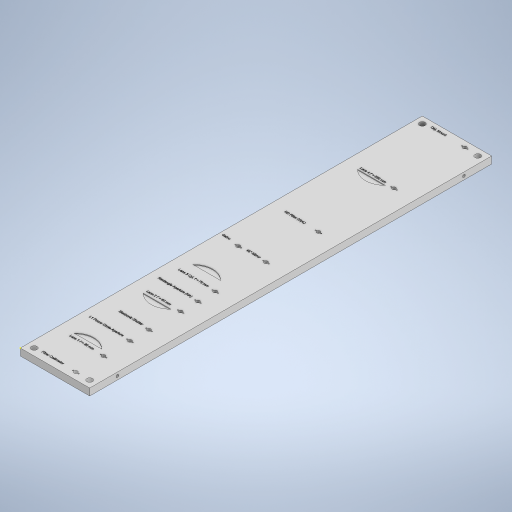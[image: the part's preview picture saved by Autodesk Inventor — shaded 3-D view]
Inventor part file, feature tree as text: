
AUTODESK INVENTOR PART (.ipt)
format: ipt  version: 2024.2 (Build 282272000, 272)  size: 3,316,224 bytes
history: native  units: in
note: dims shown in document units (in); Inventor stores cm internally (conversion verified against a paired STEP export)
features: extrude x7, sketch x5, other x2, hole x2
ambient origin geometry x8: Origin, YZ Plane, XZ Plane, XY Plane, X Axis, Y Axis, Z Axis, Center Point
bodies: Solid1 (feature_tree)
feature tree (16):
  extrude  "Extrusion1"  Depth=5.0in
  other  "Board Mounting Holes"
  extrude  "Extrusion2"  Depth=0.5in
  extrude  "Extrusion3"  Depth=0.5in
  other  "Element Holes"
  extrude  "Extrusion4"  Depth=0.5in
  extrude  "Extrusion5"  Depth=0.75in
  extrude  "Extrusion6"  Depth=0.5in
  extrude  "Extrusion7"  Depth=0.75in
  sketch  "Sketch6"  dims[d5=0.5in d6=0.5in]
  hole  "Hole1"  [1 undecoded]
  hole  "Hole2"  [1 undecoded]
  sketch  "Sketch1"  dims[d0=29.0in d1=5.0in]
  sketch  "Sketch5"  dims[d2=0.5in d3=0.0in d4=0.5in]
  sketch  "Sketch7"  dims[d7=0.5in d8=0.5in]
  sketch  "Sketch8"  dims[d9=0.4in d10=0.25in d11=0.5in d12=0.4in d13=0.3in d14=0.0in d15=0.5in d16=0.0in d17=1.5in d18=0.5in d19=0.197in d20=0.197in d21=0.25in d22=0.08in d23=0.08in d24=2.0in d25=1.898in d26=3.663in d27=1.25in d28=1.25in d29=3.667in d31=5.278in d32=6.311in d33=9.229in d34=5.107in d35=0.197in d36=0.197in d37=0.25in d38=0.08in d39=0.08in d40=0.197in d41=0.197in d42=0.25in d43=0.08in d44=0.08in d45=0.197in d46=0.197in d47=0.25in d48=0.08in d49=0.08in d50=0.197in d51=0.197in d52=0.25in d53=0.08in d54=0.08in d55=0.197in d56=0.197in d57=0.25in d58=0.08in d59=0.08in d60=0.197in d61=0.197in d62=0.25in d63=0.08in d64=0.08in d65=0.197in d66=0.197in d67=0.25in d68=0.08in d69=0.08in d70=0.197in d71=0.197in d72=0.25in d73=0.08in d74=0.08in d75=0.197in d76=0.197in d77=0.25in d78=0.08in d79=0.08in d80=0.197in d81=0.197in d82=0.25in d83=0.08in d84=0.08in d85=2.0in d86=1.0in d87=1.0in d88=1.0in d89=0.197in d90=0.197in d91=0.25in d92=0.08in d93=0.08in d94=0.197in d95=0.197in d96=0.25in d97=0.08in d98=0.08in d99=0.197in d100=0.197in d101=0.25in d102=0.08in d103=0.08in d104=0.197in d105=0.197in d106=0.25in d107=0.08in d108=0.08in d113=0.5in d114=2.0in d115=2.0in d116=2.0in d117=2.0in d118=2.0in d119=2.0in d120=2.0in d121=2.0in d122=2.0in d123=2.0in d125=1.378in d126=1.378in d127=1.378in d128=1.378in d129=1.378in d130=0.05in d131=0.0in d132=0.175in d133=0.0in d134=0.5in d135=0.0in d136=2.0in d137=1.898in d138=3.663in d139=1.25in d140=1.25in d141=3.667in d142=5.278in d144=1.58in d145=9.229in d146=5.107in d147=2.0in d148=1.0in d149=1.0in d150=1.0in d151=0.4in d152=0.4in d153=0.4in d154=0.4in d155=0.4in d156=0.4in d157=0.4in d158=0.4in d159=0.4in d160=0.4in d161=0.4in d162=0.4in d163=0.4in d164=0.4in d165=0.4in d166=0.3in d167=0.0in d168=1.5in d169=0.197in d170=0.197in d171=0.25in d172=0.08in d173=0.08in d174=1.5in d175=0.4in d176=6.311in d177=6.311in d178=6.311in d184=1.378in d185=0.197in d186=0.197in d187=0.25in d188=0.08in d189=0.08in d190=1.378in d191=2.0in d192=2.0in d193=0.196in d194=0.75in d195=0.1575in d196=0.0787in d197=90.0deg d198=0.75in d199=0.0in d200=2.0in d201=2.0in d202=0.196in d203=0.75in d204=0.1575in d205=0.0787in d206=90.0deg d207=0.75in d208=0.0in]
note: 2 required parameter values undecoded (feature->parameter linkage not recoverable at this tier; creation-order binding heuristic only, values carry confidence <= 0.55)
